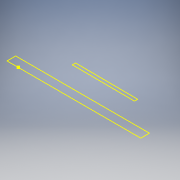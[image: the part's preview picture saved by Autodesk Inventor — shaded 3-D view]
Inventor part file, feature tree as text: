
AUTODESK INVENTOR PART (.ipt)
format: ipt  version: 2018 (Build 220112000, 112)  size: 91,648 bytes
history: native  units: mm
features: reference x8, other x6, sketch x1
ambient origin geometry x8: Origin, YZ Plane, XZ Plane, XY Plane, X Axis, Y Axis, Z Axis, Center Point
feature tree (15):
  sketch  "Sketch1"
  reference  "Reference1"
  reference  "Reference2"
  reference  "Reference3"
  reference  "Reference4"
  reference  "Reference5"
  reference  "Reference6"
  reference  "Reference7"
  reference  "Reference8"
  other  "<userpath>\OneDrive\Documents\Inventor\TSA\2018\Animatronics\Tortoise\Turtle3.iam"
  other  "Turtle3.iam"
  other  "ButtonMount:1"
  other  "ButtonMountCarrier:1"
  other  "straightBar:1"
  other  "ButtonMountLegs:1"
